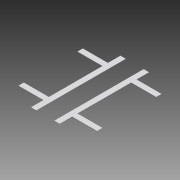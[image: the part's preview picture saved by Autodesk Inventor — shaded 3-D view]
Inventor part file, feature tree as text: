
AUTODESK INVENTOR PART (.ipt)
format: ipt  version: 2014 SP1 (Build 180222100, 222)  size: 118,784 bytes
history: native  units: in
note: dims shown in document units (in); Inventor stores cm internally (conversion verified against a paired STEP export)
features: extrude x2, sketch x2
ambient origin geometry x8: Origin, YZ Plane, XZ Plane, XY Plane, X Axis, Y Axis, Z Axis, Center Point
bodies: Solid1 (feature_tree)
feature tree (4):
  extrude  "Extrusion1"  Depth=7.0in
  extrude  "Extrusion2"  Depth=7.0in
  sketch  "Sketch1"  dims[d0=3.5in d1=7.0in]
  sketch  "Sketch2"  dims[d2=3.5in d3=7.0in d4=7.0in d5=3.5in d6=7.0in d7=3.5in d8=22.0in d9=25.0in d10=0.125in d11=0.0in d12=5.0in d13=1.5in d14=1.5in d15=1.5in d16=7.0in d17=7.0in d18=1.0in d19=0.0in]
